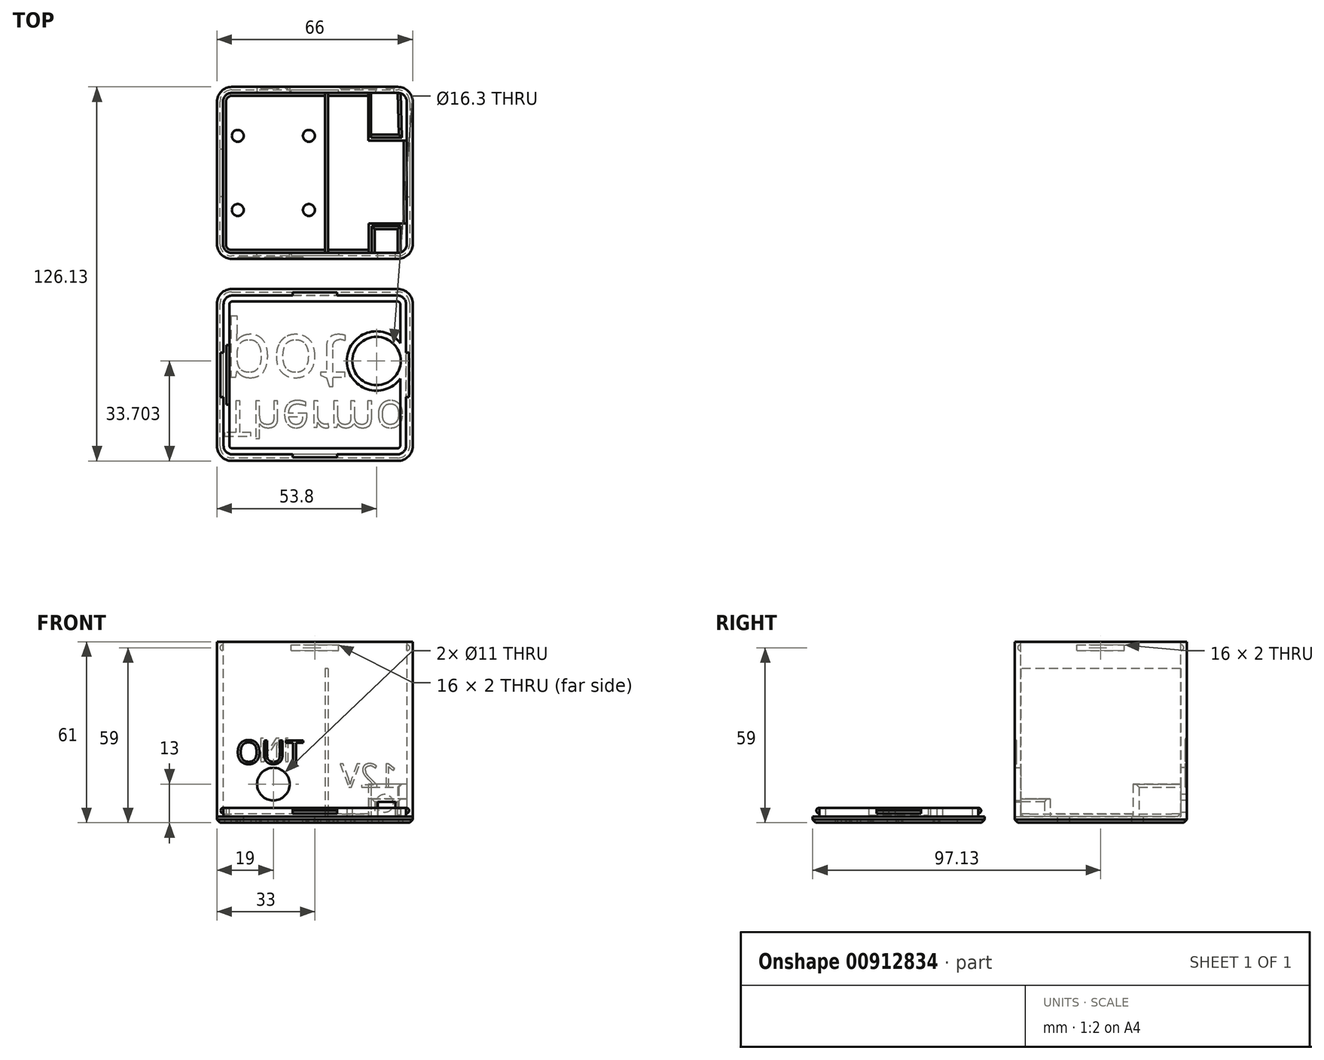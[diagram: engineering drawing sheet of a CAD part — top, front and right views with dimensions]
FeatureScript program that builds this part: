
annotation { "Feature Type Name" : "Feature", "Feature Type Description" : "" }
export const myFeature = defineFeature(function(context is Context, id is Id, definition is map)
    precondition{}
    {
        {
            assignVariable(context, id + "F0", {"name" : "box_height", "anyValue" : 59});
        }
        {
            var Q0;
            Q0=qCreatedBy(makeId("Top.planeOp"),FACE);
            var sketch = newSketch(context, id + "F1", { "sketchPlane" : qUnion([Q0])});
            skLineSegment(sketch, "E0.bottom", {"start": v(33, -29) * mm, "end": v(-33, -29) * mm});
            skLineSegment(sketch, "E0.top", {"start": v(33, 29) * mm, "end": v(-33, 29) * mm});
            skLineSegment(sketch, "E0.left", {"start": v(33, -29) * mm, "end": v(33, 29) * mm});
            skLineSegment(sketch, "E0.right", {"start": v(-33, -29) * mm, "end": v(-33, 29) * mm});
            skPoint(sketch, "E0.middle", {"position": v(0, 0) * mm});
            skLineSegment(sketch, "E1.bottom", {"start": v(33, -97.13) * mm, "end": v(-33, -97.13) * mm});
            skLineSegment(sketch, "E1.top", {"start": v(33, -39.13) * mm, "end": v(-33, -39.13) * mm});
            skLineSegment(sketch, "E1.left", {"start": v(33, -97.13) * mm, "end": v(33, -39.13) * mm});
            skLineSegment(sketch, "E1.right", {"start": v(-33, -97.13) * mm, "end": v(-33, -39.13) * mm});
            skPoint(sketch, "E1.middle", {"position": v(0, -68.13) * mm});
            skLineSegment(sketch, "E2.bottom", {"start": v(30.8, -94.93) * mm, "end": v(-30.8, -94.93) * mm});
            skLineSegment(sketch, "E2.top", {"start": v(30.8, -41.33) * mm, "end": v(-30.8, -41.33) * mm});
            skLineSegment(sketch, "E2.left", {"start": v(30.8, -94.93) * mm, "end": v(30.8, -41.33) * mm});
            skLineSegment(sketch, "E2.right", {"start": v(-30.8, -94.93) * mm, "end": v(-30.8, -41.33) * mm});
            skSolve(sketch);
        }
        {
            var Q0;
            Q0=makeQuery(id+"F1.imprint","IMPRINT",FACE,{"disambiguationData":[TD([[makeQuery(id+"F1.imprint","IMPRINT",EDGE,{"derivedFrom":sQuery(id+"F1.wireOp",EDGE,"E0.bottom")}),-1.0]])]});
            extrude(context, id + "F2", {"entities" : qUnion([Q0]), "oppositeDirection" : true, "depth" : 2 * mm, "offsetDistance" : 25 * mm});
        }
        {
            var Q0;
            Q0=makeQuery(id+"F2.opExtrude","CAP_FACE",FACE,{"disambiguationData":[OSD([sQuery(id+"F1.wireOp",EDGE,"E0.bottom"),sQuery(id+"F1.wireOp",EDGE,"E0.top"),sQuery(id+"F1.wireOp",EDGE,"E0.left"),sQuery(id+"F1.wireOp",EDGE,"E0.right")])],"isStart":true});
            extrude(context, id + "F3", {"entities" : qUnion([Q0]), "operationType" : NewBodyOperationType.ADD, "depth" : (getVariable(context, 'box_height')) * mm, "offsetDistance" : 25 * mm});
        }
        {
            var Q0;
            {var subQ0=sQuery(id+"F1.wireOp",EDGE,"E0.right");var subQ1=sQuery(id+"F1.wireOp",EDGE,"E0.top");Q0=makeQuery(id+"F3.boolean.opBoolean","MERGE",EDGE,{"derivedFrom":[makeQuery(id+"F2.opExtrude","SWEPT_EDGE",EDGE,{"disambiguationData":[OSD([subQ1,subQ0])]}),makeQuery(id+"F3.opExtrude","SWEPT_EDGE",EDGE,{"disambiguationData":[OSD([subQ1,subQ0])]})]});}
            var Q1;
            {var subQ0=sQuery(id+"F1.wireOp",EDGE,"E0.right");var subQ1=sQuery(id+"F1.wireOp",EDGE,"E0.bottom");Q1=makeQuery(id+"F3.boolean.opBoolean","MERGE",EDGE,{"derivedFrom":[makeQuery(id+"F2.opExtrude","SWEPT_EDGE",EDGE,{"disambiguationData":[OSD([subQ1,subQ0])]}),makeQuery(id+"F3.opExtrude","SWEPT_EDGE",EDGE,{"disambiguationData":[OSD([subQ1,subQ0])]})]});}
            var Q2;
            {var subQ0=sQuery(id+"F1.wireOp",EDGE,"E0.left");var subQ1=sQuery(id+"F1.wireOp",EDGE,"E0.bottom");Q2=makeQuery(id+"F3.boolean.opBoolean","MERGE",EDGE,{"derivedFrom":[makeQuery(id+"F2.opExtrude","SWEPT_EDGE",EDGE,{"disambiguationData":[OSD([subQ1,subQ0])]}),makeQuery(id+"F3.opExtrude","SWEPT_EDGE",EDGE,{"disambiguationData":[OSD([subQ1,subQ0])]})]});}
            var Q3;
            {var subQ0=sQuery(id+"F1.wireOp",EDGE,"E0.left");var subQ1=sQuery(id+"F1.wireOp",EDGE,"E0.top");Q3=makeQuery(id+"F3.boolean.opBoolean","MERGE",EDGE,{"derivedFrom":[makeQuery(id+"F2.opExtrude","SWEPT_EDGE",EDGE,{"disambiguationData":[OSD([subQ1,subQ0])]}),makeQuery(id+"F3.opExtrude","SWEPT_EDGE",EDGE,{"disambiguationData":[OSD([subQ1,subQ0])]})]});}
            fillet(context, id + "F4", {"entities" : qUnion([Q0, Q1, Q2, Q3]), "radius" : 5 * mm, "tangentPropagation" : true, "allowEdgeOverflow" : false});
        }
        {
            var Q0;
            Q0=makeQuery(id+"F3.opExtrude","CAP_FACE",FACE,{"disambiguationData":[OSD([sQuery(id+"F1.wireOp",EDGE,"E0.bottom"),sQuery(id+"F1.wireOp",EDGE,"E0.top"),sQuery(id+"F1.wireOp",EDGE,"E0.left"),sQuery(id+"F1.wireOp",EDGE,"E0.right")])],"isStart":false});
            shell(context, id + "F5", {"entities" : qUnion([Q0]), "thickness" : 2 * mm});
        }
        {
            var Q0;
            Q0=makeQuery(id+"F5.opShell","OFFSET_FACE",FACE,{"disambiguationData":[OSD([sQuery(id+"F1.wireOp",EDGE,"E0.right")])]});
            var sketch = newSketch(context, id + "F6", { "sketchPlane" : qUnion([Q0])});
            skLineSegment(sketch, "E3", {"start": v(0, 59) * mm, "end": v(0, 57) * mm});
            skPoint(sketch, "E3.endSnap0", {"position": v(0, 59) * mm});
            skLineSegment(sketch, "E4.bottom", {"start": v(8, 56) * mm, "end": v(-8, 56) * mm});
            skLineSegment(sketch, "E4.top", {"start": v(8, 58) * mm, "end": v(-8, 58) * mm});
            skLineSegment(sketch, "E4.left", {"start": v(8, 56) * mm, "end": v(8, 58) * mm});
            skLineSegment(sketch, "E4.right", {"start": v(-8, 56) * mm, "end": v(-8, 58) * mm});
            skPoint(sketch, "E4.middle", {"position": v(0, 57) * mm});
            skSolve(sketch);
        }
        {
            var Q0;
            Q0=makeQuery(id+"F5.opShell","OFFSET_FACE",FACE,{"disambiguationData":[OSD([sQuery(id+"F1.wireOp",EDGE,"E0.top")])]});
            var sketch = newSketch(context, id + "F7", { "sketchPlane" : qUnion([Q0])});
            skPoint(sketch, "E5", {"position": v(0, 59) * mm});
            skLineSegment(sketch, "E6", {"start": v(0, 59) * mm, "end": v(0, 57) * mm});
            skLineSegment(sketch, "E7.bottom", {"start": v(8, 56) * mm, "end": v(-8, 56) * mm});
            skLineSegment(sketch, "E7.top", {"start": v(8, 58) * mm, "end": v(-8, 58) * mm});
            skLineSegment(sketch, "E7.left", {"start": v(8, 56) * mm, "end": v(8, 58) * mm});
            skLineSegment(sketch, "E7.right", {"start": v(-8, 56) * mm, "end": v(-8, 58) * mm});
            skPoint(sketch, "E7.middle", {"position": v(0, 57) * mm});
            skPoint(sketch, "E8", {"position": v(-14, 11) * mm});
            skPoint(sketch, "E9", {"position": v(23.5, 4.5) * mm});
            skSolve(sketch);
        }
        {
            var Q0;
            Q0=makeQuery(id+"F7.imprint","IMPRINT",FACE,{"disambiguationData":[TD([[makeQuery(id+"F7.imprint","IMPRINT",EDGE,{"derivedFrom":sQuery(id+"F7.wireOp",EDGE,"E7.bottom")}),-1.0]])]});
            extrude(context, id + "F8", {"entities" : qUnion([Q0]), "operationType" : NewBodyOperationType.REMOVE, "oppositeDirection" : true, "depth" : 1 * mm, "offsetDistance" : 25 * mm});
        }
        {
            var Q0;
            Q0=makeQuery(id+"F6.imprint","IMPRINT",FACE,{"disambiguationData":[TD([[makeQuery(id+"F6.imprint","IMPRINT",EDGE,{"derivedFrom":sQuery(id+"F6.wireOp",EDGE,"E4.bottom")}),-1.0]])]});
            extrude(context, id + "F9", {"entities" : qUnion([Q0]), "operationType" : NewBodyOperationType.REMOVE, "oppositeDirection" : true, "depth" : 1 * mm, "offsetDistance" : 25 * mm});
        }
        {
            var Q0;
            Q0=makeQuery(id+"F5.opShell","OFFSET_FACE",FACE,{"disambiguationData":[OSD([sQuery(id+"F1.wireOp",EDGE,"E0.bottom")])]});
            var sketch = newSketch(context, id + "F10", { "sketchPlane" : qUnion([Q0])});
            skLineSegment(sketch, "E10", {"start": v(0, 59) * mm, "end": v(0, 57) * mm});
            skPoint(sketch, "E10.endSnap0", {"position": v(0, 59) * mm});
            skLineSegment(sketch, "E11.bottom", {"start": v(8, 56) * mm, "end": v(-8, 56) * mm});
            skLineSegment(sketch, "E11.top", {"start": v(8, 58) * mm, "end": v(-8, 58) * mm});
            skLineSegment(sketch, "E11.left", {"start": v(8, 56) * mm, "end": v(8, 58) * mm});
            skLineSegment(sketch, "E11.right", {"start": v(-8, 56) * mm, "end": v(-8, 58) * mm});
            skPoint(sketch, "E11.middle", {"position": v(0, 57) * mm});
            skPoint(sketch, "E12", {"position": v(14, 11) * mm});
            skLineSegment(sketch, "E13.bottom", {"start": v(-27.2, 0) * mm, "end": v(-21.2, 0) * mm});
            skLineSegment(sketch, "E13.top", {"start": v(-27.2, 5) * mm, "end": v(-21.2, 5) * mm});
            skLineSegment(sketch, "E13.left", {"start": v(-27.2, 0) * mm, "end": v(-27.2, 5) * mm});
            skLineSegment(sketch, "E13.right", {"start": v(-21.2, 0) * mm, "end": v(-21.2, 5) * mm});
            skSolve(sketch);
        }
        {
            var Q0;
            Q0=makeQuery(id+"F10.imprint","IMPRINT",FACE,{"disambiguationData":[TD([[makeQuery(id+"F10.imprint","IMPRINT",EDGE,{"derivedFrom":sQuery(id+"F10.wireOp",EDGE,"E11.bottom")}),-1.0]])]});
            extrude(context, id + "F11", {"entities" : qUnion([Q0]), "operationType" : NewBodyOperationType.REMOVE, "oppositeDirection" : true, "depth" : 1 * mm, "offsetDistance" : 25 * mm});
        }
        {
            var Q0;
            Q0=makeQuery(id+"F5.opShell","OFFSET_FACE",FACE,{"disambiguationData":[OSD([sQuery(id+"F1.wireOp",EDGE,"E0.left")])]});
            var sketch = newSketch(context, id + "F12", { "sketchPlane" : qUnion([Q0])});
            skLineSegment(sketch, "E14", {"start": v(0, 59) * mm, "end": v(0, 57) * mm});
            skPoint(sketch, "E14.endSnap0", {"position": v(0, 59) * mm});
            skLineSegment(sketch, "E15.bottom", {"start": v(8, 56) * mm, "end": v(-8, 56) * mm});
            skLineSegment(sketch, "E15.top", {"start": v(8, 58) * mm, "end": v(-8, 58) * mm});
            skLineSegment(sketch, "E15.left", {"start": v(8, 56) * mm, "end": v(8, 58) * mm});
            skLineSegment(sketch, "E15.right", {"start": v(-8, 56) * mm, "end": v(-8, 58) * mm});
            skPoint(sketch, "E15.middle", {"position": v(0, 57) * mm});
            skSolve(sketch);
        }
        {
            var Q0;
            Q0=makeQuery(id+"F12.imprint","IMPRINT",FACE,{"disambiguationData":[TD([[makeQuery(id+"F12.imprint","IMPRINT",EDGE,{"derivedFrom":sQuery(id+"F12.wireOp",EDGE,"E15.bottom")}),-1.0]])]});
            extrude(context, id + "F13", {"entities" : qUnion([Q0]), "operationType" : NewBodyOperationType.REMOVE, "oppositeDirection" : true, "depth" : 1 * mm, "offsetDistance" : 25 * mm});
        }
        {
            var Q0;
            Q0=makeQuery(id+"F1.imprint","IMPRINT",FACE,{"disambiguationData":[TD([[makeQuery(id+"F1.imprint","IMPRINT",EDGE,{"derivedFrom":sQuery(id+"F1.wireOp",EDGE,"E1.bottom")}),-1.0]])]});
            var Q1;
            Q1=makeQuery(id+"F1.imprint","IMPRINT",FACE,{"disambiguationData":[TD([[makeQuery(id+"F1.imprint","IMPRINT",EDGE,{"derivedFrom":sQuery(id+"F1.wireOp",EDGE,"E2.bottom")}),-1.0]])]});
            var Q2;
            Q2=makeQuery(id+"F1.imprint","IMPRINT",FACE,{"disambiguationData":[TD([[makeQuery(id+"F1.imprint","IMPRINT",EDGE,{"derivedFrom":sQuery(id+"F1.wireOp",EDGE,"IM9Et3MU-YbXc-tv5d-9tDR-dDhzX9vFgJBc.bottom")}),-1.0]])]});
            extrude(context, id + "F14", {"entities" : qUnion([Q0, Q1, Q2]), "oppositeDirection" : true, "depth" : 2 * mm, "offsetDistance" : 25 * mm});
        }
        {
            var Q0;
            Q0=makeQuery(id+"F14.opExtrude","SWEPT_EDGE",EDGE,{"disambiguationData":[OSD([sQuery(id+"F1.wireOp",EDGE,"E1.bottom"),sQuery(id+"F1.wireOp",EDGE,"E1.right")])]});
            var Q1;
            Q1=makeQuery(id+"F14.opExtrude","SWEPT_EDGE",EDGE,{"disambiguationData":[OSD([sQuery(id+"F1.wireOp",EDGE,"E1.top"),sQuery(id+"F1.wireOp",EDGE,"E1.right")])]});
            var Q2;
            Q2=makeQuery(id+"F14.opExtrude","SWEPT_EDGE",EDGE,{"disambiguationData":[OSD([sQuery(id+"F1.wireOp",EDGE,"E1.bottom"),sQuery(id+"F1.wireOp",EDGE,"E1.left")])]});
            var Q3;
            Q3=makeQuery(id+"F14.opExtrude","SWEPT_EDGE",EDGE,{"disambiguationData":[OSD([sQuery(id+"F1.wireOp",EDGE,"E1.top"),sQuery(id+"F1.wireOp",EDGE,"E1.left")])]});
            fillet(context, id + "F15", {"entities" : qUnion([Q0, Q1, Q2, Q3]), "radius" : 5 * mm, "tangentPropagation" : true, "allowEdgeOverflow" : false});
        }
        {
            var Q0;
            Q0=makeQuery(id+"F1.imprint","IMPRINT",FACE,{"disambiguationData":[TD([[makeQuery(id+"F1.imprint","IMPRINT",EDGE,{"derivedFrom":sQuery(id+"F1.wireOp",EDGE,"E2.bottom")}),-1.0]])]});
            extrude(context, id + "F16", {"entities" : qUnion([Q0]), "operationType" : NewBodyOperationType.ADD, "depth" : 3 * mm, "offsetDistance" : 25 * mm});
        }
        {
            var Q0;
            Q0=makeQuery(id+"F16.opExtrude","SWEPT_EDGE",EDGE,{"disambiguationData":[OSD([sQuery(id+"F1.wireOp",EDGE,"E2.bottom"),sQuery(id+"F1.wireOp",EDGE,"E2.right")])]});
            var Q1;
            Q1=makeQuery(id+"F16.opExtrude","SWEPT_EDGE",EDGE,{"disambiguationData":[OSD([sQuery(id+"F1.wireOp",EDGE,"E2.bottom"),sQuery(id+"F1.wireOp",EDGE,"E2.left")])]});
            var Q2;
            Q2=makeQuery(id+"F16.opExtrude","SWEPT_EDGE",EDGE,{"disambiguationData":[OSD([sQuery(id+"F1.wireOp",EDGE,"E2.top"),sQuery(id+"F1.wireOp",EDGE,"E2.left")])]});
            var Q3;
            Q3=makeQuery(id+"F16.opExtrude","SWEPT_EDGE",EDGE,{"disambiguationData":[OSD([sQuery(id+"F1.wireOp",EDGE,"E2.top"),sQuery(id+"F1.wireOp",EDGE,"E2.right")])]});
            fillet(context, id + "F17", {"entities" : qUnion([Q0, Q1, Q2, Q3]), "radius" : 3 * mm, "tangentPropagation" : true, "allowEdgeOverflow" : false});
        }
        {
            var Q0;
            Q0=makeQuery(id+"F16.opExtrude","CAP_FACE",FACE,{"disambiguationData":[OSD([sQuery(id+"F1.wireOp",EDGE,"E2.bottom"),sQuery(id+"F1.wireOp",EDGE,"E2.top"),sQuery(id+"F1.wireOp",EDGE,"E2.left"),sQuery(id+"F1.wireOp",EDGE,"E2.right")])],"isStart":false});
            shell(context, id + "F18", {"entities" : qUnion([Q0]), "thickness" : 2 * mm});
        }
        {
            var Q0;
            Q0=makeQuery(id+"F16.opExtrude","SWEPT_FACE",FACE,{"disambiguationData":[OSD([sQuery(id+"F1.wireOp",EDGE,"E2.bottom")])]});
            var sketch = newSketch(context, id + "F19", { "sketchPlane" : qUnion([Q0])});
            skLineSegment(sketch, "E16", {"start": v(0, 3) * mm, "end": v(0, 2.05) * mm});
            skPoint(sketch, "E16.endSnap0", {"position": v(0, 3) * mm});
            skLineSegment(sketch, "E17.bottom", {"start": v(7.5, 1.1) * mm, "end": v(-7.5, 1.1) * mm});
            skLineSegment(sketch, "E17.top", {"start": v(7.5, 3) * mm, "end": v(-7.5, 3) * mm});
            skLineSegment(sketch, "E17.left", {"start": v(7.5, 1.1) * mm, "end": v(7.5, 3) * mm});
            skLineSegment(sketch, "E17.right", {"start": v(-7.5, 1.1) * mm, "end": v(-7.5, 3) * mm});
            skPoint(sketch, "E17.middle", {"position": v(0, 2.05) * mm});
            skSolve(sketch);
        }
        {
            var Q0;
            Q0=makeQuery(id+"F19.imprint","IMPRINT",FACE,{"disambiguationData":[TD([[makeQuery(id+"F19.imprint","IMPRINT",EDGE,{"derivedFrom":sQuery(id+"F19.wireOp",EDGE,"E17.bottom")}),-1.0]])]});
            extrude(context, id + "F20", {"entities" : qUnion([Q0]), "operationType" : NewBodyOperationType.ADD, "depth" : 1 * mm, "offsetDistance" : 25 * mm});
        }
        {
            var Q0;
            Q0=makeQuery(id+"F16.opExtrude","SWEPT_FACE",FACE,{"disambiguationData":[OSD([sQuery(id+"F1.wireOp",EDGE,"E2.right")])]});
            var sketch = newSketch(context, id + "F21", { "sketchPlane" : qUnion([Q0])});
            skLineSegment(sketch, "E18", {"start": v(68.13, 3) * mm, "end": v(68.13, 2.05) * mm});
            skLineSegment(sketch, "E19.bottom", {"start": v(75.63, 1.1) * mm, "end": v(60.63, 1.1) * mm});
            skLineSegment(sketch, "E19.top", {"start": v(75.63, 3) * mm, "end": v(60.63, 3) * mm});
            skLineSegment(sketch, "E19.left", {"start": v(75.63, 1.1) * mm, "end": v(75.63, 3) * mm});
            skLineSegment(sketch, "E19.right", {"start": v(60.63, 1.1) * mm, "end": v(60.63, 3) * mm});
            skPoint(sketch, "E19.middle", {"position": v(68.13, 2.05) * mm});
            skSolve(sketch);
        }
        {
            var Q0;
            Q0=makeQuery(id+"F21.imprint","IMPRINT",FACE,{"disambiguationData":[TD([[makeQuery(id+"F21.imprint","IMPRINT",EDGE,{"derivedFrom":sQuery(id+"F21.wireOp",EDGE,"E19.bottom")}),-1.0]])]});
            extrude(context, id + "F22", {"entities" : qUnion([Q0]), "operationType" : NewBodyOperationType.ADD, "depth" : 1 * mm, "offsetDistance" : 25 * mm});
        }
        {
            var Q0;
            Q0=makeQuery(id+"F16.opExtrude","SWEPT_FACE",FACE,{"disambiguationData":[OSD([sQuery(id+"F1.wireOp",EDGE,"E2.left")])]});
            var sketch = newSketch(context, id + "F23", { "sketchPlane" : qUnion([Q0])});
            skLineSegment(sketch, "E20", {"start": v(-68.13, 3) * mm, "end": v(-68.13, 2.05) * mm});
            skLineSegment(sketch, "E21.bottom", {"start": v(-60.63, 1.1) * mm, "end": v(-75.63, 1.1) * mm});
            skLineSegment(sketch, "E21.top", {"start": v(-60.63, 3) * mm, "end": v(-75.63, 3) * mm});
            skLineSegment(sketch, "E21.left", {"start": v(-60.63, 1.1) * mm, "end": v(-60.63, 3) * mm});
            skLineSegment(sketch, "E21.right", {"start": v(-75.63, 1.1) * mm, "end": v(-75.63, 3) * mm});
            skPoint(sketch, "E21.middle", {"position": v(-68.13, 2.05) * mm});
            skSolve(sketch);
        }
        {
            var Q0;
            Q0=makeQuery(id+"F23.imprint","IMPRINT",FACE,{"disambiguationData":[TD([[makeQuery(id+"F23.imprint","IMPRINT",EDGE,{"derivedFrom":sQuery(id+"F23.wireOp",EDGE,"E21.bottom")}),-1.0]])]});
            extrude(context, id + "F24", {"entities" : qUnion([Q0]), "operationType" : NewBodyOperationType.ADD, "depth" : 1 * mm, "offsetDistance" : 25 * mm});
        }
        {
            var Q0;
            Q0=makeQuery(id+"F16.opExtrude","SWEPT_FACE",FACE,{"disambiguationData":[OSD([sQuery(id+"F1.wireOp",EDGE,"E2.top")])]});
            var sketch = newSketch(context, id + "F25", { "sketchPlane" : qUnion([Q0])});
            skLineSegment(sketch, "E22", {"start": v(0, 3) * mm, "end": v(0, 2.05) * mm});
            skPoint(sketch, "E22.endSnap0", {"position": v(0, 3) * mm});
            skLineSegment(sketch, "E23.bottom", {"start": v(7.5, 1.1) * mm, "end": v(-7.5, 1.1) * mm});
            skLineSegment(sketch, "E23.top", {"start": v(7.5, 3) * mm, "end": v(-7.5, 3) * mm});
            skLineSegment(sketch, "E23.left", {"start": v(7.5, 1.1) * mm, "end": v(7.5, 3) * mm});
            skLineSegment(sketch, "E23.right", {"start": v(-7.5, 1.1) * mm, "end": v(-7.5, 3) * mm});
            skPoint(sketch, "E23.middle", {"position": v(0, 2.05) * mm});
            skSolve(sketch);
        }
        {
            var Q0;
            Q0=makeQuery(id+"F25.imprint","IMPRINT",FACE,{"disambiguationData":[TD([[makeQuery(id+"F25.imprint","IMPRINT",EDGE,{"derivedFrom":sQuery(id+"F25.wireOp",EDGE,"E23.bottom")}),-1.0]])]});
            extrude(context, id + "F26", {"entities" : qUnion([Q0]), "operationType" : NewBodyOperationType.ADD, "depth" : 1 * mm, "offsetDistance" : 25 * mm});
        }
        {
            var Q0;
            Q0=makeQuery(id+"F8.boolean.opBoolean","COPY",EDGE,{"derivedFrom":makeQuery(id+"F8.opExtrude","CAP_EDGE",EDGE,{"disambiguationData":[OSD([sQuery(id+"F7.wireOp",EDGE,"E7.bottom")])],"isStart":false})});
            var Q1;
            Q1=makeQuery(id+"F8.boolean.opBoolean","COPY",EDGE,{"derivedFrom":makeQuery(id+"F8.opExtrude","CAP_EDGE",EDGE,{"disambiguationData":[OSD([sQuery(id+"F7.wireOp",EDGE,"E7.top")])],"isStart":false})});
            var Q2;
            Q2=makeQuery(id+"F13.boolean.opBoolean","COPY",EDGE,{"derivedFrom":makeQuery(id+"F13.opExtrude","CAP_EDGE",EDGE,{"disambiguationData":[OSD([sQuery(id+"F12.wireOp",EDGE,"E15.bottom")])],"isStart":false})});
            var Q3;
            Q3=makeQuery(id+"F13.boolean.opBoolean","COPY",EDGE,{"derivedFrom":makeQuery(id+"F13.opExtrude","CAP_EDGE",EDGE,{"disambiguationData":[OSD([sQuery(id+"F12.wireOp",EDGE,"E15.top")])],"isStart":false})});
            var Q4;
            Q4=makeQuery(id+"F11.boolean.opBoolean","COPY",EDGE,{"derivedFrom":makeQuery(id+"F11.opExtrude","CAP_EDGE",EDGE,{"disambiguationData":[OSD([sQuery(id+"F10.wireOp",EDGE,"E11.bottom")])],"isStart":false})});
            var Q5;
            Q5=makeQuery(id+"F11.boolean.opBoolean","COPY",EDGE,{"derivedFrom":makeQuery(id+"F11.opExtrude","CAP_EDGE",EDGE,{"disambiguationData":[OSD([sQuery(id+"F10.wireOp",EDGE,"E11.top")])],"isStart":false})});
            var Q6;
            Q6=makeQuery(id+"F9.boolean.opBoolean","COPY",EDGE,{"derivedFrom":makeQuery(id+"F9.opExtrude","CAP_EDGE",EDGE,{"disambiguationData":[OSD([sQuery(id+"F6.wireOp",EDGE,"E4.bottom")])],"isStart":false})});
            var Q7;
            Q7=makeQuery(id+"F9.boolean.opBoolean","COPY",EDGE,{"derivedFrom":makeQuery(id+"F9.opExtrude","CAP_EDGE",EDGE,{"disambiguationData":[OSD([sQuery(id+"F6.wireOp",EDGE,"E4.top")])],"isStart":false})});
            var Q8;
            Q8=makeQuery(id+"F26.opExtrude","CAP_EDGE",EDGE,{"disambiguationData":[OSD([sQuery(id+"F25.wireOp",EDGE,"E23.top")])],"isStart":false});
            var Q9;
            Q9=makeQuery(id+"F26.opExtrude","CAP_EDGE",EDGE,{"disambiguationData":[OSD([sQuery(id+"F25.wireOp",EDGE,"E23.bottom")])],"isStart":false});
            var Q10;
            Q10=makeQuery(id+"F24.opExtrude","CAP_EDGE",EDGE,{"disambiguationData":[OSD([sQuery(id+"F23.wireOp",EDGE,"E21.bottom")])],"isStart":false});
            var Q11;
            Q11=makeQuery(id+"F24.opExtrude","CAP_EDGE",EDGE,{"disambiguationData":[OSD([sQuery(id+"F23.wireOp",EDGE,"E21.top")])],"isStart":false});
            var Q12;
            Q12=makeQuery(id+"F20.opExtrude","CAP_EDGE",EDGE,{"disambiguationData":[OSD([sQuery(id+"F19.wireOp",EDGE,"E17.bottom")])],"isStart":false});
            var Q13;
            Q13=makeQuery(id+"F20.opExtrude","CAP_EDGE",EDGE,{"disambiguationData":[OSD([sQuery(id+"F19.wireOp",EDGE,"E17.top")])],"isStart":false});
            var Q14;
            Q14=makeQuery(id+"F22.opExtrude","CAP_EDGE",EDGE,{"disambiguationData":[OSD([sQuery(id+"F21.wireOp",EDGE,"E19.bottom")])],"isStart":false});
            var Q15;
            Q15=makeQuery(id+"F22.opExtrude","CAP_EDGE",EDGE,{"disambiguationData":[OSD([sQuery(id+"F21.wireOp",EDGE,"E19.top")])],"isStart":false});
            fillet(context, id + "F27", {"entities" : qUnion([Q0, Q1, Q2, Q3, Q4, Q5, Q6, Q7, Q8, Q9, Q10, Q11, Q12, Q13, Q14, Q15]), "radius" : 1 * mm, "tangentPropagation" : true, "allowEdgeOverflow" : false});
        }
        {
            var Q0;
            Q0=makeQuery(id+"F14.opExtrude","CAP_FACE",FACE,{"disambiguationData":[OSD([sQuery(id+"F1.wireOp",EDGE,"E1.bottom"),sQuery(id+"F1.wireOp",EDGE,"E1.top"),sQuery(id+"F1.wireOp",EDGE,"E1.left"),sQuery(id+"F1.wireOp",EDGE,"E1.right")])],"isStart":false});
            var sketch = newSketch(context, id + "F28", { "sketchPlane" : qUnion([Q0])});
            skText(sketch, "E24", { "text": "Thermo", "fontName": "OpenSans-Regular.ttf"});
            skText(sketch, "E25", { "text": "pot", "fontName": "OpenSans-Regular.ttf"});
            skPoint(sketch, "E26", {"position": v(20.8, 63.43) * mm});
            skCircle(sketch, "E27", {"center": v(20.8, 63.43) * mm, "radius": 10 * mm});
            const initialGuessF28  = {"E24": [-0.03062, 0.0769, 1, 0, 0.012], "E25": [-0.03062, 0.0547, 1, 0, 0.019]};
            skSetInitialGuess(sketch, initialGuessF28);
            skSolve(sketch);
        }
        {
            var Q0;
            Q0=makeQuery(id+"F28.imprint","IMPRINT",FACE,{"disambiguationData":[TD([[makeQuery(id+"F28.imprint","IMPRINT",EDGE,{"derivedFrom":sQuery(id+"F28.wireOp",EDGE,"E24.sketch_text.stroke-0")}),-1.0]])]});
            var Q1;
            Q1=makeQuery(id+"F28.imprint","IMPRINT",FACE,{"disambiguationData":[TD([[makeQuery(id+"F28.imprint","IMPRINT",EDGE,{"derivedFrom":sQuery(id+"F28.wireOp",EDGE,"E24.sketch_text.stroke-8")}),-1.0]])]});
            var Q2;
            Q2=makeQuery(id+"F28.imprint","IMPRINT",FACE,{"disambiguationData":[TD([[makeQuery(id+"F28.imprint","IMPRINT",EDGE,{"derivedFrom":sQuery(id+"F28.wireOp",EDGE,"E24.sketch_text.stroke-45")}),-1.0]])]});
            var Q3;
            Q3=makeQuery(id+"F28.imprint","IMPRINT",FACE,{"disambiguationData":[TD([[makeQuery(id+"F28.imprint","IMPRINT",EDGE,{"derivedFrom":sQuery(id+"F28.wireOp",EDGE,"E24.sketch_text.stroke-58")}),-1.0]])]});
            var Q4;
            Q4=makeQuery(id+"F28.imprint","IMPRINT",FACE,{"disambiguationData":[TD([[makeQuery(id+"F28.imprint","IMPRINT",EDGE,{"derivedFrom":sQuery(id+"F28.wireOp",EDGE,"E25.sketch_text.stroke-42")}),-1.0]])]});
            var Q5;
            Q5=makeQuery(id+"F28.imprint","IMPRINT",FACE,{"disambiguationData":[TD([[makeQuery(id+"F28.imprint","IMPRINT",EDGE,{"derivedFrom":sQuery(id+"F28.wireOp",EDGE,"E24.sketch_text.stroke-26")}),-1.0]])]});
            var Q6;
            Q6=makeQuery(id+"F28.imprint","IMPRINT",FACE,{"disambiguationData":[TD([[makeQuery(id+"F28.imprint","IMPRINT",EDGE,{"derivedFrom":sQuery(id+"F28.wireOp",EDGE,"E24.sketch_text.stroke-86")}),-1.0]])]});
            var Q7;
            Q7=makeQuery(id+"F28.imprint","IMPRINT",FACE,{"disambiguationData":[TD([[makeQuery(id+"F28.imprint","IMPRINT",EDGE,{"derivedFrom":sQuery(id+"F28.wireOp",EDGE,"E25.sketch_text.stroke-0")}),-1.0]])]});
            var Q8;
            Q8=makeQuery(id+"F28.imprint","IMPRINT",FACE,{"disambiguationData":[TD([[makeQuery(id+"F28.imprint","IMPRINT",EDGE,{"derivedFrom":sQuery(id+"F28.wireOp",EDGE,"E25.sketch_text.stroke-25")}),-1.0]])]});
            extrude(context, id + "F29", {"entities" : qUnion([Q0, Q1, Q2, Q3, Q4, Q5, Q6, Q7, Q8]), "operationType" : NewBodyOperationType.REMOVE, "oppositeDirection" : true, "depth" : 1 * mm, "offsetDistance" : 25 * mm});
        }
        {
            var Q0;
            Q0=makeQuery(id+"F5.opShell","OFFSET_FACE",FACE,{"disambiguationData":[OSD([sQuery(id+"F1.wireOp",EDGE,"E0.bottom"),sQuery(id+"F1.wireOp",EDGE,"E0.top"),sQuery(id+"F1.wireOp",EDGE,"E0.left"),sQuery(id+"F1.wireOp",EDGE,"E0.right")])]});
            var sketch = newSketch(context, id + "F30", { "sketchPlane" : qUnion([Q0])});
            skLineSegment(sketch, "E28.bottom", {"start": v(3.5, 27) * mm, "end": v(4.5, 27) * mm});
            skLineSegment(sketch, "E28.top", {"start": v(3.5, -27) * mm, "end": v(4.5, -27) * mm});
            skLineSegment(sketch, "E28.left", {"start": v(3.5, 27) * mm, "end": v(3.5, -27) * mm});
            skLineSegment(sketch, "E28.right", {"start": v(4.5, 27) * mm, "end": v(4.5, -27) * mm});
            skPoint(sketch, "E29", {"position": v(-14, 0) * mm});
            skLineSegment(sketch, "E30.bottom", {"start": v(-2, -12.5) * mm, "end": v(-26, -12.5) * mm});
            skLineSegment(sketch, "E30.top", {"start": v(-2, 12.5) * mm, "end": v(-26, 12.5) * mm});
            skLineSegment(sketch, "E30.left", {"start": v(-2, -12.5) * mm, "end": v(-2, 12.5) * mm});
            skLineSegment(sketch, "E30.right", {"start": v(-26, -12.5) * mm, "end": v(-26, 12.5) * mm});
            skPoint(sketch, "E31", {"position": v(-26, 12.5) * mm});
            skPoint(sketch, "E32", {"position": v(-2, 12.5) * mm});
            skPoint(sketch, "E33", {"position": v(-2, -12.5) * mm});
            skPoint(sketch, "E34", {"position": v(-26, -12.5) * mm});
            skLineSegment(sketch, "E35.bottom", {"start": v(31, 12.9) * mm, "end": v(19, 12.9) * mm});
            skLineSegment(sketch, "E35.top", {"start": v(31, 27) * mm, "end": v(19, 27) * mm});
            skLineSegment(sketch, "E35.left", {"start": v(31, 12.9) * mm, "end": v(31, 27) * mm});
            skLineSegment(sketch, "E35.right", {"start": v(19, 12.9) * mm, "end": v(19, 27) * mm});
            skLineSegment(sketch, "E36.bottom", {"start": v(31, 27) * mm, "end": v(18, 27) * mm});
            skLineSegment(sketch, "E36.top", {"start": v(31, 10.9) * mm, "end": v(18, 10.9) * mm});
            skLineSegment(sketch, "E36.left", {"start": v(31, 27) * mm, "end": v(31, 10.9) * mm});
            skLineSegment(sketch, "E36.right", {"start": v(18, 27) * mm, "end": v(18, 10.9) * mm});
            skLineSegment(sketch, "E37", {"start": v(28, 27) * mm, "end": v(28.37, 12.9) * mm});
            skLineSegment(sketch, "E38", {"start": v(20.2, -27) * mm, "end": v(20.2, -19) * mm});
            skLineSegment(sketch, "E39", {"start": v(20.2, -19) * mm, "end": v(31, -19) * mm});
            skLineSegment(sketch, "E40", {"start": v(31, -19) * mm, "end": v(31, -17) * mm});
            skLineSegment(sketch, "E41", {"start": v(31, -17) * mm, "end": v(18.2, -17) * mm});
            skLineSegment(sketch, "E42", {"start": v(18.2, -17) * mm, "end": v(18.2, -27) * mm});
            skLineSegment(sketch, "E43", {"start": v(18.2, -27) * mm, "end": v(20.2, -27) * mm});
            skLineSegment(sketch, "E44", {"start": v(28, -27) * mm, "end": v(28, -19) * mm});
            skSolve(sketch);
        }
        {
            var Q0;
            Q0=makeQuery(id+"F30.imprint","IMPRINT",FACE,{"disambiguationData":[TD([[makeQuery(id+"F30.imprint","IMPRINT",EDGE,{"derivedFrom":sQuery(id+"F30.wireOp",EDGE,"E28.bottom")}),1.0]])]});
            extrude(context, id + "F31", {"entities" : qUnion([Q0]), "operationType" : NewBodyOperationType.ADD, "depth" : 50 * mm, "offsetDistance" : 25 * mm});
        }
        {
            var Q0;
            Q0=sQuery(id+"F7.wireOp",VERTEX,"E8");
            var Q1;
            Q1=makeQuery(id+"F2.opExtrude","SWEPT_BODY",BODY,{"disambiguationData":[OSD([sQuery(id+"F1.wireOp",EDGE,"E0.bottom"),sQuery(id+"F1.wireOp",EDGE,"E0.top"),sQuery(id+"F1.wireOp",EDGE,"E0.left"),sQuery(id+"F1.wireOp",EDGE,"E0.right")])]});
            hole(context, id + "F32", {"style" : HoleStyle.SIMPLE, "endStyle" : HoleEndStyle.BLIND, "holeDiameter" : 11 * mm, "majorDiameter" : 5 * mm, "holeDepth" : 3 * mm, "isTappedThrough" : true, "tappedDepth" : 12 * mm, "tapClearance" : 3, "locations" : qUnion([Q0]), "scope" : qUnion([Q1])});
        }
        {
            var Q0;
            Q0=sQuery(id+"F10.wireOp",VERTEX,"E12");
            var Q1;
            Q1=makeQuery(id+"F2.opExtrude","SWEPT_BODY",BODY,{"disambiguationData":[OSD([sQuery(id+"F1.wireOp",EDGE,"E0.bottom"),sQuery(id+"F1.wireOp",EDGE,"E0.top"),sQuery(id+"F1.wireOp",EDGE,"E0.left"),sQuery(id+"F1.wireOp",EDGE,"E0.right")])]});
            var Q2;
            Q2=makeQuery(id+"F14.opExtrude","SWEPT_BODY",BODY,{"disambiguationData":[OSD([sQuery(id+"F1.wireOp",EDGE,"E1.bottom"),sQuery(id+"F1.wireOp",EDGE,"E1.top"),sQuery(id+"F1.wireOp",EDGE,"E1.left"),sQuery(id+"F1.wireOp",EDGE,"E1.right")])]});
            hole(context, id + "F33", {"style" : HoleStyle.SIMPLE, "endStyle" : HoleEndStyle.BLIND, "holeDiameter" : 11 * mm, "majorDiameter" : 5 * mm, "holeDepth" : 3 * mm, "isTappedThrough" : true, "tappedDepth" : 12 * mm, "tapClearance" : 3, "locations" : qUnion([Q0]), "scope" : qUnion([Q1, Q2])});
        }
        {
            var Q0;
            Q0=sQuery(id+"F30.wireOp",VERTEX,"E31");
            var Q1;
            Q1=sQuery(id+"F30.wireOp",VERTEX,"E32");
            var Q2;
            Q2=sQuery(id+"F30.wireOp",VERTEX,"E33");
            var Q3;
            Q3=sQuery(id+"F30.wireOp",VERTEX,"E34");
            var Q4;
            Q4=makeQuery(id+"F2.opExtrude","SWEPT_BODY",BODY,{"disambiguationData":[OSD([sQuery(id+"F1.wireOp",EDGE,"E0.bottom"),sQuery(id+"F1.wireOp",EDGE,"E0.top"),sQuery(id+"F1.wireOp",EDGE,"E0.left"),sQuery(id+"F1.wireOp",EDGE,"E0.right")])]});
            hole(context, id + "F34", {"style" : HoleStyle.SIMPLE, "endStyle" : HoleEndStyle.BLIND, "holeDiameter" : 4 * mm, "majorDiameter" : 5 * mm, "holeDepth" : 3 * mm, "isTappedThrough" : true, "tappedDepth" : 12 * mm, "tapClearance" : 3, "locations" : qUnion([Q0, Q1, Q2, Q3]), "scope" : qUnion([Q4])});
        }
        {
            var Q0;
            Q0=sQuery(id+"F7.wireOp",VERTEX,"E9");
            var Q1;
            Q1=sQuery(id+"F7.wireOp",VERTEX,"516fc9de-c8e2-4aeb-a09b-7aa7388f7c0a");
            var Q2;
            Q2=makeQuery(id+"F2.opExtrude","SWEPT_BODY",BODY,{"disambiguationData":[OSD([sQuery(id+"F1.wireOp",EDGE,"E0.bottom"),sQuery(id+"F1.wireOp",EDGE,"E0.top"),sQuery(id+"F1.wireOp",EDGE,"E0.left"),sQuery(id+"F1.wireOp",EDGE,"E0.right")])]});
            hole(context, id + "F35", {"style" : HoleStyle.SIMPLE, "endStyle" : HoleEndStyle.BLIND, "holeDiameter" : 6 * mm, "majorDiameter" : 5 * mm, "holeDepth" : 3 * mm, "isTappedThrough" : true, "tappedDepth" : 12 * mm, "tapClearance" : 3, "locations" : qUnion([Q0, Q1]), "scope" : qUnion([Q2])});
        }
        {
            var Q0;
            Q0=makeQuery(id+"F28.imprint","IMPRINT",FACE,{"disambiguationData":[TD([[makeQuery(id+"F28.imprint","IMPRINT",EDGE,{"derivedFrom":sQuery(id+"F28.wireOp",EDGE,"E27")}),1.0]])]});
            extrude(context, id + "F36", {"entities" : qUnion([Q0]), "operationType" : NewBodyOperationType.ADD, "oppositeDirection" : true, "depth" : 5 * mm, "offsetDistance" : 25 * mm});
        }
        {
            var Q0;
            Q0=sQuery(id+"F28.wireOp",VERTEX,"E26");
            var Q1;
            Q1=makeQuery(id+"F14.opExtrude","SWEPT_BODY",BODY,{"disambiguationData":[OSD([sQuery(id+"F1.wireOp",EDGE,"E1.bottom"),sQuery(id+"F1.wireOp",EDGE,"E1.top"),sQuery(id+"F1.wireOp",EDGE,"E1.left"),sQuery(id+"F1.wireOp",EDGE,"E1.right")])]});
            hole(context, id + "F37", {"style" : HoleStyle.SIMPLE, "endStyle" : HoleEndStyle.BLIND, "holeDiameter" : 16.3 * mm, "majorDiameter" : 5 * mm, "holeDepth" : 6 * mm, "isTappedThrough" : true, "tappedDepth" : 12 * mm, "tapClearance" : 3, "locations" : qUnion([Q0]), "scope" : qUnion([Q1])});
        }
        {
            var Q0;
            {var subQ1=sQuery(id+"F30.wireOp",EDGE,"E35.right");Q0=makeQuery(id+"F30.imprint","IMPRINT",FACE,{"disambiguationData":[TD([[makeQuery(id+"F30.imprint","IMPRINT",EDGE,{"derivedFrom":subQ1}),1.0]])]});}
            var Q1;
            {var subQ3=sQuery(id+"F30.wireOp",EDGE,"E37");Q1=makeQuery(id+"F30.imprint","IMPRINT",FACE,{"disambiguationData":[TD([[makeQuery(id+"F30.imprint","IMPRINT",EDGE,{"derivedFrom":subQ3}),1.0]])]});}
            extrude(context, id + "F38", {"entities" : qUnion([Q0, Q1]), "operationType" : NewBodyOperationType.ADD, "depth" : 11 * mm, "offsetDistance" : 25 * mm});
        }
        {
            var Q0;
            {var subQ4=sQuery(id+"F30.wireOp",EDGE,"E44");Q0=makeQuery(id+"F30.imprint","IMPRINT",FACE,{"disambiguationData":[TD([[makeQuery(id+"F30.imprint","IMPRINT",EDGE,{"derivedFrom":subQ4}),-1.0]])]});}
            var Q1;
            {var subQ4=sQuery(id+"F30.wireOp",EDGE,"E38");Q1=makeQuery(id+"F30.imprint","IMPRINT",FACE,{"disambiguationData":[TD([[makeQuery(id+"F30.imprint","IMPRINT",EDGE,{"derivedFrom":subQ4}),1.0]])]});}
            extrude(context, id + "F39", {"entities" : qUnion([Q0, Q1]), "operationType" : NewBodyOperationType.ADD, "depth" : 6 * mm, "offsetDistance" : 25 * mm});
        }
        {
            var Q0;
            Q0=makeQuery(id+"F10.imprint","IMPRINT",FACE,{"disambiguationData":[TD([[makeQuery(id+"F10.imprint","IMPRINT",EDGE,{"derivedFrom":sQuery(id+"F10.wireOp",EDGE,"E13.bottom")}),1.0]])]});
            extrude(context, id + "F40", {"entities" : qUnion([Q0]), "operationType" : NewBodyOperationType.REMOVE, "endBound" : BoundingType.UP_TO_NEXT, "oppositeDirection" : true, "depth" : 25 * mm, "offsetDistance" : 25 * mm});
        }
        {
            var Q0;
            {var subQ0=sQuery(id+"F1.wireOp",EDGE,"E0.bottom");Q0=makeQuery(id+"F3.boolean.opBoolean","MERGE",FACE,{"derivedFrom":[makeQuery(id+"F2.opExtrude","SWEPT_FACE",FACE,{"disambiguationData":[OSD([subQ0])]}),makeQuery(id+"F3.opExtrude","SWEPT_FACE",FACE,{"disambiguationData":[OSD([subQ0])]})]});}
            var sketch = newSketch(context, id + "F41", { "sketchPlane" : qUnion([Q0])});
            skText(sketch, "E45", { "text": "OUT", "fontName": "OpenSans-Regular.ttf"});
            const initialGuessF41  = {"E45": [-0.02666, 0.01782, 1, 0, 0.008]};
            skSetInitialGuess(sketch, initialGuessF41);
            skSolve(sketch);
        }
        {
            var Q0;
            Q0 = qSketchRegion(id + "F41", true);
            extrude(context, id + "F42", {"entities" : qUnion([Q0]), "operationType" : NewBodyOperationType.REMOVE, "oppositeDirection" : true, "depth" : 0.5 * mm, "offsetDistance" : 25 * mm});
        }
        {
            var Q0;
            {var subQ0=sQuery(id+"F1.wireOp",EDGE,"E0.top");Q0=makeQuery(id+"F3.boolean.opBoolean","MERGE",FACE,{"derivedFrom":[makeQuery(id+"F2.opExtrude","SWEPT_FACE",FACE,{"disambiguationData":[OSD([subQ0])]}),makeQuery(id+"F3.opExtrude","SWEPT_FACE",FACE,{"disambiguationData":[OSD([subQ0])]})]});}
            var sketch = newSketch(context, id + "F43", { "sketchPlane" : qUnion([Q0])});
            skText(sketch, "E46", { "text": "IN", "fontName": "OpenSans-Regular.ttf"});
            skText(sketch, "E47", { "text": "12V", "fontName": "OpenSans-Regular.ttf"});
            const initialGuessF43  = {"E46": [0.00786, 0.01853, 1, 0, 0.008], "E47": [-0.0279, 0.0099, 1, 0, 0.008]};
            skSetInitialGuess(sketch, initialGuessF43);
            skSolve(sketch);
        }
        {
            var Q0;
            Q0 = qSketchRegion(id + "F43", true);
            extrude(context, id + "F44", {"entities" : qUnion([Q0]), "operationType" : NewBodyOperationType.REMOVE, "oppositeDirection" : true, "depth" : 0.5 * mm, "offsetDistance" : 25 * mm});
        }
        {
            var Q0;
            Q0=makeQuery(id+"F2.opExtrude","CAP_EDGE",EDGE,{"disambiguationData":[OSD([sQuery(id+"F1.wireOp",EDGE,"E0.bottom")])],"isStart":false});
            var Q1;
            Q1=makeQuery(id+"F14.opExtrude","CAP_EDGE",EDGE,{"disambiguationData":[OSD([sQuery(id+"F1.wireOp",EDGE,"E1.bottom")])],"isStart":false});
            var Q2;
            {var subQ1=sQuery(id+"F1.wireOp",EDGE,"E0.top");Q2=makeQuery(id+"F31.boolean.opBoolean","SPLIT",EDGE,{"disambiguationData":[TD([makeQuery(id+"F31.opExtrude","SWEPT_FACE",FACE,{"disambiguationData":[OSD([sQuery(id+"F30.wireOp",EDGE,"E28.left")])]})])],"derivedFrom":makeQuery(id+"F5.opShell","OFFSET_EDGE",EDGE,{"disambiguationData":[OSD([subQ1]),TDD([makeQuery(id+"F2.opExtrude","CAP_EDGE",EDGE,{"disambiguationData":[OSD([subQ1])],"isStart":false})])]})});}
            var Q3;
            {var subQ1=sQuery(id+"F1.wireOp",EDGE,"E0.bottom");var subQ4=makeQuery(id+"F31.opExtrude","SWEPT_FACE",FACE,{"disambiguationData":[OSD([sQuery(id+"F30.wireOp",EDGE,"E28.right")])]});Q3=makeQuery(id+"F39.boolean.opBoolean","SPLIT",EDGE,{"disambiguationData":[TD([subQ4])],"derivedFrom":makeQuery(id+"F31.boolean.opBoolean","SPLIT",EDGE,{"disambiguationData":[TD([subQ4])],"derivedFrom":makeQuery(id+"F5.opShell","OFFSET_EDGE",EDGE,{"disambiguationData":[OSD([subQ1]),TDD([makeQuery(id+"F2.opExtrude","CAP_EDGE",EDGE,{"disambiguationData":[OSD([subQ1])],"isStart":false})])]})})});}
            var Q4;
            {var subQ0=sQuery(id+"F1.wireOp",EDGE,"E0.left");Q4=makeQuery(id+"F5.opShell","OFFSET_EDGE",EDGE,{"disambiguationData":[OSD([subQ0]),TDD([makeQuery(id+"F2.opExtrude","CAP_EDGE",EDGE,{"disambiguationData":[OSD([subQ0])],"isStart":false})])]});}
            var Q5;
            {var subQ1=sQuery(id+"F1.wireOp",EDGE,"E0.top");var subQ4=makeQuery(id+"F31.opExtrude","SWEPT_FACE",FACE,{"disambiguationData":[OSD([sQuery(id+"F30.wireOp",EDGE,"E28.right")])]});Q5=makeQuery(id+"F38.boolean.opBoolean","SPLIT",EDGE,{"disambiguationData":[TD([subQ4])],"derivedFrom":makeQuery(id+"F31.boolean.opBoolean","SPLIT",EDGE,{"disambiguationData":[TD([subQ4])],"derivedFrom":makeQuery(id+"F5.opShell","OFFSET_EDGE",EDGE,{"disambiguationData":[OSD([subQ1]),TDD([makeQuery(id+"F2.opExtrude","CAP_EDGE",EDGE,{"disambiguationData":[OSD([subQ1])],"isStart":false})])]})})});}
            var Q6;
            Q6=makeQuery(id+"F39.opExtrude","CAP_EDGE",EDGE,{"disambiguationData":[OSD([sQuery(id+"F30.wireOp",EDGE,"E38")])],"isStart":false});
            var Q7;
            Q7=makeQuery(id+"F39.opExtrude","CAP_EDGE",EDGE,{"disambiguationData":[OSD([sQuery(id+"F30.wireOp",EDGE,"E44")])],"isStart":false});
            var Q8;
            Q8=makeQuery(id+"F39.opExtrude","CAP_EDGE",EDGE,{"disambiguationData":[OSD([sQuery(id+"F30.wireOp",EDGE,"E39")])],"isStart":false});
            var Q9;
            Q9=makeQuery(id+"F38.opExtrude","CAP_EDGE",EDGE,{"disambiguationData":[OSD([sQuery(id+"F30.wireOp",EDGE,"E37")])],"isStart":false});
            var Q10;
            Q10=makeQuery(id+"F38.opExtrude","CAP_EDGE",EDGE,{"disambiguationData":[OSD([sQuery(id+"F30.wireOp",EDGE,"E35.bottom")])],"isStart":false});
            chamfer(context, id + "F45", {"entities" : qUnion([Q0, Q1, Q2, Q3, Q4, Q5, Q6, Q7, Q8, Q9, Q10]), "width" : 1 * mm, "tangentPropagation" : true});
        }
        {
            var Q0;
            Q0=makeQuery(id+"F36.boolean.opBoolean","MERGE",FACE,{"derivedFrom":[makeQuery(id+"F26.boolean.opBoolean","MERGE",FACE,{"derivedFrom":[makeQuery(id+"F24.boolean.opBoolean","MERGE",FACE,{"derivedFrom":[makeQuery(id+"F22.boolean.opBoolean","MERGE",FACE,{"derivedFrom":[makeQuery(id+"F20.boolean.opBoolean","MERGE",FACE,{"derivedFrom":[makeQuery(id+"F16.opExtrude","CAP_FACE",FACE,{"disambiguationData":[OSD([sQuery(id+"F1.wireOp",EDGE,"E2.bottom"),sQuery(id+"F1.wireOp",EDGE,"E2.top"),sQuery(id+"F1.wireOp",EDGE,"E2.left"),sQuery(id+"F1.wireOp",EDGE,"E2.right")])],"isStart":false}),makeQuery(id+"F20.opExtrude","SWEPT_FACE",FACE,{"disambiguationData":[OSD([sQuery(id+"F19.wireOp",EDGE,"E17.top")])]})]}),makeQuery(id+"F22.opExtrude","SWEPT_FACE",FACE,{"disambiguationData":[OSD([sQuery(id+"F21.wireOp",EDGE,"E19.top")])]})]}),makeQuery(id+"F24.opExtrude","SWEPT_FACE",FACE,{"disambiguationData":[OSD([sQuery(id+"F23.wireOp",EDGE,"E21.top")])]})]}),makeQuery(id+"F26.opExtrude","SWEPT_FACE",FACE,{"disambiguationData":[OSD([sQuery(id+"F25.wireOp",EDGE,"E23.top")])]})]}),makeQuery(id+"F36.opExtrude","CAP_FACE",FACE,{"disambiguationData":[OSD([sQuery(id+"F28.wireOp",EDGE,"E27")])],"isStart":false})]});
            var sketch = newSketch(context, id + "F46", { "sketchPlane" : qUnion([Q0])});
            skLineSegment(sketch, "E48.bottom", {"start": v(-28.8, -68.13) * mm, "end": v(-29.8, -68.13) * mm});
            skLineSegment(sketch, "E48.top", {"start": v(-28.8, -58.13) * mm, "end": v(-29.8, -58.13) * mm});
            skLineSegment(sketch, "E48.left", {"start": v(-28.8, -68.13) * mm, "end": v(-28.8, -58.13) * mm});
            skLineSegment(sketch, "E48.right", {"start": v(-29.8, -68.13) * mm, "end": v(-29.8, -58.13) * mm});
            skLineSegment(sketch, "E49.MirrorCS", {"start": v(-29.8, -68.13) * mm, "end": v(-29.8, -78.13) * mm});
            skLineSegment(sketch, "E50.MirrorCS", {"start": v(-28.8, -78.13) * mm, "end": v(-29.8, -78.13) * mm});
            skLineSegment(sketch, "E51.MirrorCS", {"start": v(-28.8, -68.13) * mm, "end": v(-28.8, -78.13) * mm});
            skSolve(sketch);
        }
        {
            var Q0;
            Q0=makeQuery(id+"F46.imprint","IMPRINT",FACE,{"disambiguationData":[TD([[makeQuery(id+"F46.imprint","IMPRINT",EDGE,{"derivedFrom":sQuery(id+"F46.wireOp",EDGE,"E48.bottom")}),1.0]])]});
            var Q1;
            Q1=makeQuery(id+"F46.imprint","IMPRINT",FACE,{"disambiguationData":[TD([[makeQuery(id+"F46.imprint","IMPRINT",EDGE,{"derivedFrom":sQuery(id+"F46.wireOp",EDGE,"E48.bottom")}),-1.0]])]});
            extrude(context, id + "F47", {"entities" : qUnion([Q0, Q1]), "operationType" : NewBodyOperationType.REMOVE, "oppositeDirection" : true, "depth" : 2.5 * mm, "offsetDistance" : 25 * mm});
        }
    });
